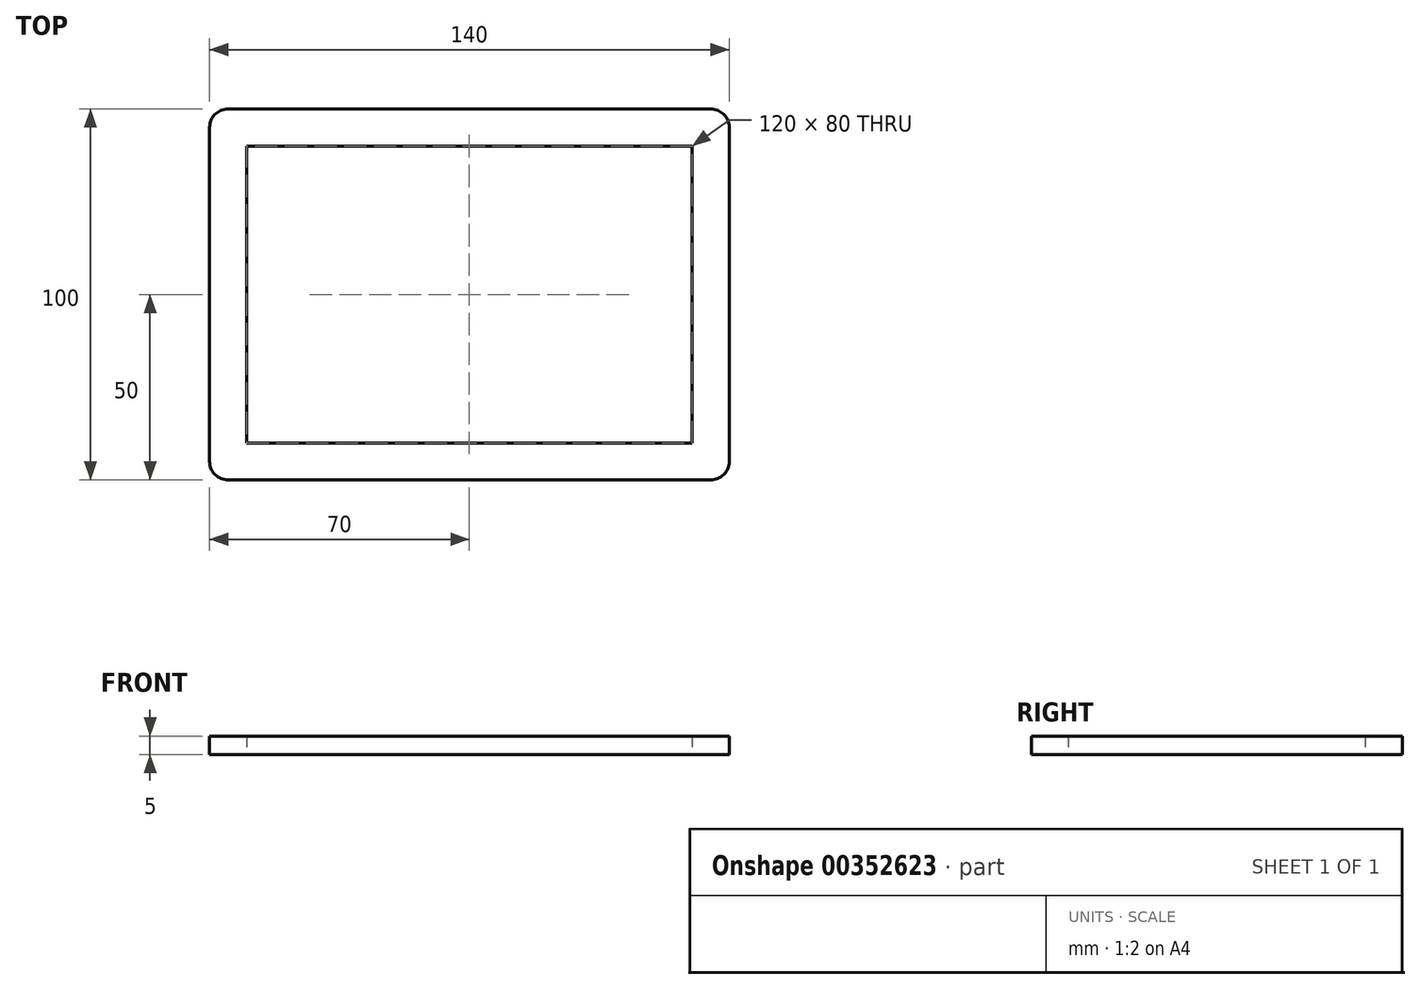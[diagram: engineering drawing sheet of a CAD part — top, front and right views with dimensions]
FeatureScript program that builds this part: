
annotation { "Feature Type Name" : "Feature", "Feature Type Description" : "" }
export const myFeature = defineFeature(function(context is Context, id is Id, definition is map)
    precondition{}
    {
        {
            var Q0;
            Q0=qCreatedBy(makeId("Top.planeOp"),FACE);
            var sketch = newSketch(context, id + "F0", { "sketchPlane" : qUnion([Q0])});
            skLineSegment(sketch, "E0.bottom", {"start": v(65, 50) * mm, "end": v(-65, 50) * mm});
            skLineSegment(sketch, "E0.top", {"start": v(65, -50) * mm, "end": v(-65, -50) * mm});
            skLineSegment(sketch, "E0.left", {"start": v(70, 45) * mm, "end": v(70, -45) * mm});
            skLineSegment(sketch, "E0.right", {"start": v(-70, 45) * mm, "end": v(-70, -45) * mm});
            skPoint(sketch, "E0.middle", {"position": v(0, 0) * mm});
            skPoint(sketch, "E1.visualSharp", {"position": v(-70, 50) * mm});
            skArc(sketch, "E1.filletArc", {"start": v(-65, 50) * mm, "mid": v(-68.54, 48.54) * mm, "end": v(-70, 45) * mm});
            skPoint(sketch, "E2.visualSharp", {"position": v(70, 50) * mm});
            skArc(sketch, "E2.filletArc", {"start": v(70, 45) * mm, "mid": v(68.54, 48.54) * mm, "end": v(65, 50) * mm});
            skPoint(sketch, "E3.visualSharp", {"position": v(70, -50) * mm});
            skArc(sketch, "E3.filletArc", {"start": v(65, -50) * mm, "mid": v(68.54, -48.54) * mm, "end": v(70, -45) * mm});
            skPoint(sketch, "E4.visualSharp", {"position": v(-70, -50) * mm});
            skArc(sketch, "E4.filletArc", {"start": v(-70, -45) * mm, "mid": v(-68.54, -48.54) * mm, "end": v(-65, -50) * mm});
            skLineSegment(sketch, "E5.bottom", {"start": v(60, -40) * mm, "end": v(-60, -40) * mm});
            skLineSegment(sketch, "E5.top", {"start": v(60, 40) * mm, "end": v(-60, 40) * mm});
            skLineSegment(sketch, "E5.left", {"start": v(60, -40) * mm, "end": v(60, 40) * mm});
            skLineSegment(sketch, "E5.right", {"start": v(-60, -40) * mm, "end": v(-60, 40) * mm});
            skSolve(sketch);
        }
        {
            var Q0;
            Q0=qSketchRegion(id+"F0",true);
            extrude(context, id + "F1", {"entities" : qUnion([Q0]), "depth" : 5 * mm});
        }
    });
